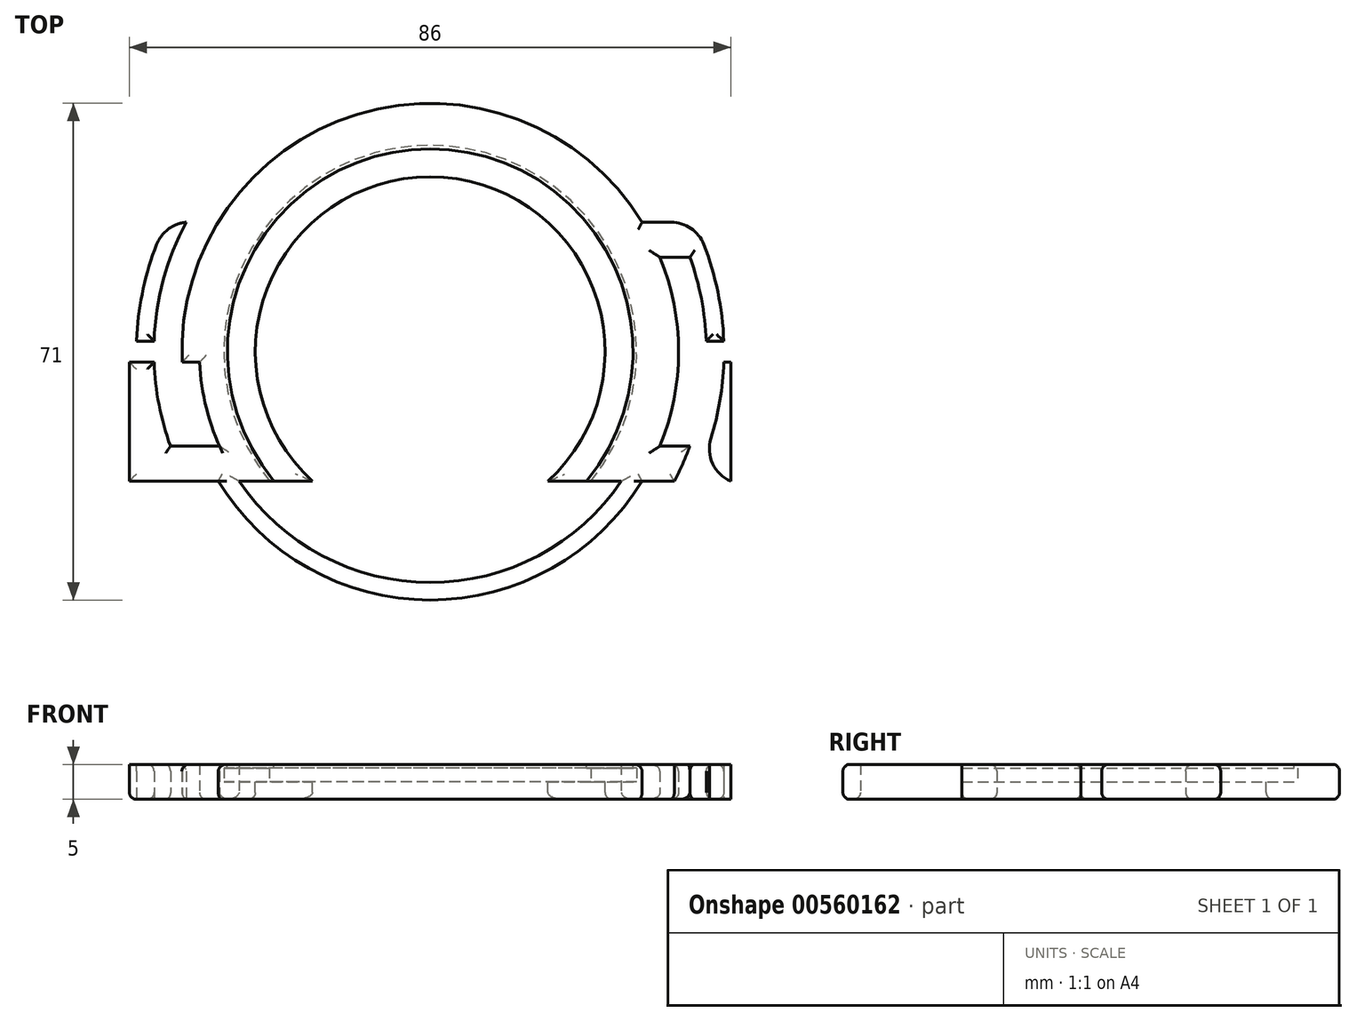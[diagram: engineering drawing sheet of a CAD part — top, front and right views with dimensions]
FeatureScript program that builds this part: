
annotation { "Feature Type Name" : "Feature", "Feature Type Description" : "" }
export const myFeature = defineFeature(function(context is Context, id is Id, definition is map)
    precondition{}
    {
        {
            var Q0;
            Q0=qCreatedBy(makeId("Top.planeOp"),FACE);
            var sketch = newSketch(context, id + "F0", { "sketchPlane" : qUnion([Q0])});
            skCircle(sketch, "E0", {"center": v(0, 0) * mm, "radius": 33 * mm});
            skLineSegment(sketch, "E1.bottom", {"start": v(43, -18.5) * mm, "end": v(-43, -18.5) * mm});
            skLineSegment(sketch, "E1.top", {"start": v(43, 18.5) * mm, "end": v(-43, 18.5) * mm});
            skLineSegment(sketch, "E1.left", {"start": v(43, -18.5) * mm, "end": v(43, 18.5) * mm});
            skLineSegment(sketch, "E1.right", {"start": v(-43, -18.5) * mm, "end": v(-43, 18.5) * mm});
            skCircle(sketch, "E2", {"center": v(0, 0) * mm, "radius": 42 * mm});
            skCircle(sketch, "E3", {"center": v(0, 0) * mm, "radius": 35.5 * mm});
            skCircle(sketch, "E4", {"center": v(0, 0) * mm, "radius": 39.5 * mm});
            skLineSegment(sketch, "E5.bottom", {"start": v(38.5, 13.5) * mm, "end": v(-38.5, 13.5) * mm});
            skLineSegment(sketch, "E5.top", {"start": v(38.5, -13.5) * mm, "end": v(-38.5, -13.5) * mm});
            skLineSegment(sketch, "E5.left", {"start": v(38.5, 13.5) * mm, "end": v(38.5, -13.5) * mm});
            skLineSegment(sketch, "E5.right", {"start": v(-38.5, 13.5) * mm, "end": v(-38.5, -13.5) * mm});
            skLineSegment(sketch, "E6.bottom", {"start": v(50, 1.5) * mm, "end": v(-50, 1.5) * mm});
            skLineSegment(sketch, "E6.top", {"start": v(50, -1.5) * mm, "end": v(-50, -1.5) * mm});
            skLineSegment(sketch, "E6.left", {"start": v(50, 1.5) * mm, "end": v(50, -1.5) * mm});
            skLineSegment(sketch, "E6.right", {"start": v(-50, 1.5) * mm, "end": v(-50, -1.5) * mm});
            skSolve(sketch);
        }
        {
            var Q0;
            {var subQ6=sQuery(id+"F0.wireOp",EDGE,"E1.bottom");var subQ14=sQuery(id+"F0.wireOp",EDGE,"E2");var subQ16=makeQuery(id+"F0.imprint","INTERSECT",VERTEX,{"disambiguationData":[OD(1.0)],"derivedFrom":[subQ6,subQ14]});Q0=makeQuery(id+"F0.imprint","IMPRINT",FACE,{"disambiguationData":[TD([[makeQuery(id+"F0.imprint","IMPRINT",EDGE,{"disambiguationData":[TD([[subQ16,1.0]])],"derivedFrom":subQ6}),-1.0]])]});}
            var Q1;
            {var subQ0=sQuery(id+"F0.wireOp",EDGE,"E5.bottom");var subQ1=sQuery(id+"F0.wireOp",EDGE,"E4");var subQ2=makeQuery(id+"F0.imprint","INTERSECT",VERTEX,{"disambiguationData":[OD(1.0)],"derivedFrom":[subQ1,subQ0]});Q1=makeQuery(id+"F0.imprint","IMPRINT",FACE,{"disambiguationData":[TD([[makeQuery(id+"F0.imprint","IMPRINT",EDGE,{"disambiguationData":[TD([[subQ2,-1.0]])],"derivedFrom":subQ1}),-1.0]])]});}
            var Q2;
            {var subQ0=sQuery(id+"F0.wireOp",EDGE,"E5.right");var subQ1=sQuery(id+"F0.wireOp",EDGE,"E4");var subQ2=makeQuery(id+"F0.imprint","INTERSECT",VERTEX,{"disambiguationData":[OD(1.0)],"derivedFrom":[subQ1,subQ0]});Q2=makeQuery(id+"F0.imprint","IMPRINT",FACE,{"disambiguationData":[TD([[makeQuery(id+"F0.imprint","IMPRINT",EDGE,{"disambiguationData":[TD([[subQ2,-1.0]])],"derivedFrom":subQ1}),-1.0]])]});}
            var Q3;
            {var subQ0=sQuery(id+"F0.wireOp",EDGE,"E3");var subQ1=sQuery(id+"F0.wireOp",EDGE,"E1.top");var subQ2=makeQuery(id+"F0.imprint","INTERSECT",VERTEX,{"disambiguationData":[OD(1.0)],"derivedFrom":[subQ1,subQ0]});Q3=makeQuery(id+"F0.imprint","IMPRINT",FACE,{"disambiguationData":[TD([[makeQuery(id+"F0.imprint","IMPRINT",EDGE,{"disambiguationData":[TD([[subQ2,-1.0]])],"derivedFrom":subQ1}),1.0]])]});}
            var Q4;
            {var subQ0=sQuery(id+"F0.wireOp",EDGE,"E3");var subQ1=sQuery(id+"F0.wireOp",EDGE,"E1.bottom");var subQ2=makeQuery(id+"F0.imprint","INTERSECT",VERTEX,{"disambiguationData":[OD(1.0)],"derivedFrom":[subQ1,subQ0]});Q4=makeQuery(id+"F0.imprint","IMPRINT",FACE,{"disambiguationData":[TD([[makeQuery(id+"F0.imprint","IMPRINT",EDGE,{"disambiguationData":[TD([[subQ2,-1.0]])],"derivedFrom":subQ1}),-1.0]])]});}
            var Q5;
            {var subQ0=sQuery(id+"F0.wireOp",EDGE,"E5.bottom");var subQ1=sQuery(id+"F0.wireOp",EDGE,"E0");var subQ2=makeQuery(id+"F0.imprint","INTERSECT",VERTEX,{"disambiguationData":[OD(1.0)],"derivedFrom":[subQ1,subQ0]});Q5=makeQuery(id+"F0.imprint","IMPRINT",FACE,{"disambiguationData":[TD([[makeQuery(id+"F0.imprint","IMPRINT",EDGE,{"disambiguationData":[TD([[subQ2,-1.0]])],"derivedFrom":subQ1}),-1.0]])]});}
            var Q6;
            {var subQ0=sQuery(id+"F0.wireOp",EDGE,"E5.top");var subQ1=sQuery(id+"F0.wireOp",EDGE,"E0");var subQ2=makeQuery(id+"F0.imprint","INTERSECT",VERTEX,{"disambiguationData":[OD(0.0)],"derivedFrom":[subQ1,subQ0]});Q6=makeQuery(id+"F0.imprint","IMPRINT",FACE,{"disambiguationData":[TD([[makeQuery(id+"F0.imprint","IMPRINT",EDGE,{"disambiguationData":[TD([[subQ2,-1.0]])],"derivedFrom":subQ1}),-1.0]])]});}
            var Q7;
            {var subQ0=sQuery(id+"F0.wireOp",EDGE,"E1.top");var subQ1=sQuery(id+"F0.wireOp",EDGE,"E0");var subQ2=makeQuery(id+"F0.imprint","INTERSECT",VERTEX,{"disambiguationData":[OD(1.0)],"derivedFrom":[subQ1,subQ0]});Q7=makeQuery(id+"F0.imprint","IMPRINT",FACE,{"disambiguationData":[TD([[makeQuery(id+"F0.imprint","IMPRINT",EDGE,{"disambiguationData":[TD([[subQ2,-1.0]])],"derivedFrom":subQ1}),-1.0]])]});}
            var Q8;
            {var subQ0=sQuery(id+"F0.wireOp",EDGE,"E1.bottom");var subQ1=sQuery(id+"F0.wireOp",EDGE,"E0");var subQ2=makeQuery(id+"F0.imprint","INTERSECT",VERTEX,{"disambiguationData":[OD(0.0)],"derivedFrom":[subQ1,subQ0]});Q8=makeQuery(id+"F0.imprint","IMPRINT",FACE,{"disambiguationData":[TD([[makeQuery(id+"F0.imprint","IMPRINT",EDGE,{"disambiguationData":[TD([[subQ2,-1.0]])],"derivedFrom":subQ1}),-1.0]])]});}
            var Q9;
            {var subQ0=sQuery(id+"F0.wireOp",EDGE,"E1.top");var subQ1=sQuery(id+"F0.wireOp",EDGE,"E0");var subQ2=makeQuery(id+"F0.imprint","INTERSECT",VERTEX,{"disambiguationData":[OD(0.0)],"derivedFrom":[subQ1,subQ0]});Q9=makeQuery(id+"F0.imprint","IMPRINT",FACE,{"disambiguationData":[TD([[makeQuery(id+"F0.imprint","IMPRINT",EDGE,{"disambiguationData":[TD([[subQ2,-1.0]])],"derivedFrom":subQ1}),-1.0]])]});}
            var Q10;
            {var subQ0=sQuery(id+"F0.wireOp",EDGE,"E1.top");var subQ1=sQuery(id+"F0.wireOp",EDGE,"E0");var subQ2=makeQuery(id+"F0.imprint","INTERSECT",VERTEX,{"disambiguationData":[OD(0.0)],"derivedFrom":[subQ1,subQ0]});Q10=makeQuery(id+"F0.imprint","IMPRINT",FACE,{"disambiguationData":[TD([[makeQuery(id+"F0.imprint","IMPRINT",EDGE,{"disambiguationData":[TD([[subQ2,-1.0]])],"derivedFrom":subQ1}),1.0]])]});}
            var Q11;
            {var subQ0=sQuery(id+"F0.wireOp",EDGE,"E1.top");var subQ1=sQuery(id+"F0.wireOp",EDGE,"E0");var subQ2=makeQuery(id+"F0.imprint","INTERSECT",VERTEX,{"disambiguationData":[OD(0.0)],"derivedFrom":[subQ1,subQ0]});Q11=makeQuery(id+"F0.imprint","IMPRINT",FACE,{"disambiguationData":[TD([[makeQuery(id+"F0.imprint","IMPRINT",EDGE,{"disambiguationData":[TD([[subQ2,1.0]])],"derivedFrom":subQ1}),1.0]])]});}
            var Q12;
            {var subQ0=sQuery(id+"F0.wireOp",EDGE,"E5.bottom");var subQ1=sQuery(id+"F0.wireOp",EDGE,"E0");var subQ2=makeQuery(id+"F0.imprint","INTERSECT",VERTEX,{"disambiguationData":[OD(1.0)],"derivedFrom":[subQ1,subQ0]});Q12=makeQuery(id+"F0.imprint","IMPRINT",FACE,{"disambiguationData":[TD([[makeQuery(id+"F0.imprint","IMPRINT",EDGE,{"disambiguationData":[TD([[subQ2,-1.0]])],"derivedFrom":subQ1}),1.0]])]});}
            var Q13;
            {var subQ0=sQuery(id+"F0.wireOp",EDGE,"E5.top");var subQ1=sQuery(id+"F0.wireOp",EDGE,"E0");var subQ2=makeQuery(id+"F0.imprint","INTERSECT",VERTEX,{"disambiguationData":[OD(0.0)],"derivedFrom":[subQ1,subQ0]});Q13=makeQuery(id+"F0.imprint","IMPRINT",FACE,{"disambiguationData":[TD([[makeQuery(id+"F0.imprint","IMPRINT",EDGE,{"disambiguationData":[TD([[subQ2,-1.0]])],"derivedFrom":subQ1}),1.0]])]});}
            var Q14;
            {var subQ0=sQuery(id+"F0.wireOp",EDGE,"E1.bottom");var subQ1=sQuery(id+"F0.wireOp",EDGE,"E0");var subQ2=makeQuery(id+"F0.imprint","INTERSECT",VERTEX,{"disambiguationData":[OD(0.0)],"derivedFrom":[subQ1,subQ0]});Q14=makeQuery(id+"F0.imprint","IMPRINT",FACE,{"disambiguationData":[TD([[makeQuery(id+"F0.imprint","IMPRINT",EDGE,{"disambiguationData":[TD([[subQ2,-1.0]])],"derivedFrom":subQ1}),1.0]])]});}
            var Q15;
            {var subQ0=sQuery(id+"F0.wireOp",EDGE,"E5.bottom");var subQ1=sQuery(id+"F0.wireOp",EDGE,"E4");var subQ2=makeQuery(id+"F0.imprint","INTERSECT",VERTEX,{"disambiguationData":[OD(0.0)],"derivedFrom":[subQ1,subQ0]});Q15=makeQuery(id+"F0.imprint","IMPRINT",FACE,{"disambiguationData":[TD([[makeQuery(id+"F0.imprint","IMPRINT",EDGE,{"disambiguationData":[TD([[subQ2,1.0]])],"derivedFrom":subQ1}),-1.0]])]});}
            var Q16;
            {var subQ0=sQuery(id+"F0.wireOp",EDGE,"E1.top");var subQ1=sQuery(id+"F0.wireOp",EDGE,"E0");var subQ2=makeQuery(id+"F0.imprint","INTERSECT",VERTEX,{"disambiguationData":[OD(0.0)],"derivedFrom":[subQ1,subQ0]});Q16=makeQuery(id+"F0.imprint","IMPRINT",FACE,{"disambiguationData":[TD([[makeQuery(id+"F0.imprint","IMPRINT",EDGE,{"disambiguationData":[TD([[subQ2,1.0]])],"derivedFrom":subQ1}),-1.0]])]});}
            var Q17;
            {var subQ0=sQuery(id+"F0.wireOp",EDGE,"E4");var subQ1=sQuery(id+"F0.wireOp",EDGE,"E1.top");var subQ2=makeQuery(id+"F0.imprint","INTERSECT",VERTEX,{"disambiguationData":[OD(0.0)],"derivedFrom":[subQ1,subQ0]});Q17=makeQuery(id+"F0.imprint","IMPRINT",FACE,{"disambiguationData":[TD([[makeQuery(id+"F0.imprint","IMPRINT",EDGE,{"disambiguationData":[TD([[subQ2,-1.0]])],"derivedFrom":subQ1}),1.0]])]});}
            var Q18;
            {var subQ0=sQuery(id+"F0.wireOp",EDGE,"E5.top");var subQ1=sQuery(id+"F0.wireOp",EDGE,"E4");var subQ2=makeQuery(id+"F0.imprint","INTERSECT",VERTEX,{"disambiguationData":[OD(1.0)],"derivedFrom":[subQ1,subQ0]});Q18=makeQuery(id+"F0.imprint","IMPRINT",FACE,{"disambiguationData":[TD([[makeQuery(id+"F0.imprint","IMPRINT",EDGE,{"disambiguationData":[TD([[subQ2,-1.0]])],"derivedFrom":subQ1}),-1.0]])]});}
            var Q19;
            {var subQ6=sQuery(id+"F0.wireOp",EDGE,"E2");var subQ7=sQuery(id+"F0.wireOp",EDGE,"E1.bottom");var subQ8=makeQuery(id+"F0.imprint","INTERSECT",VERTEX,{"disambiguationData":[OD(0.0)],"derivedFrom":[subQ7,subQ6]});Q19=makeQuery(id+"F0.imprint","IMPRINT",FACE,{"disambiguationData":[TD([[makeQuery(id+"F0.imprint","IMPRINT",EDGE,{"disambiguationData":[TD([[subQ8,-1.0]])],"derivedFrom":subQ7}),-1.0]])]});}
            var Q20;
            {var subQ0=sQuery(id+"F0.wireOp",EDGE,"E1.bottom");var subQ1=sQuery(id+"F0.wireOp",EDGE,"E0");var subQ2=makeQuery(id+"F0.imprint","INTERSECT",VERTEX,{"disambiguationData":[OD(1.0)],"derivedFrom":[subQ1,subQ0]});Q20=makeQuery(id+"F0.imprint","IMPRINT",FACE,{"disambiguationData":[TD([[makeQuery(id+"F0.imprint","IMPRINT",EDGE,{"disambiguationData":[TD([[subQ2,-1.0]])],"derivedFrom":subQ1}),-1.0]])]});}
            var Q21;
            {var subQ0=sQuery(id+"F0.wireOp",EDGE,"E4");var subQ1=sQuery(id+"F0.wireOp",EDGE,"E1.bottom");var subQ2=makeQuery(id+"F0.imprint","INTERSECT",VERTEX,{"disambiguationData":[OD(0.0)],"derivedFrom":[subQ1,subQ0]});Q21=makeQuery(id+"F0.imprint","IMPRINT",FACE,{"disambiguationData":[TD([[makeQuery(id+"F0.imprint","IMPRINT",EDGE,{"disambiguationData":[TD([[subQ2,-1.0]])],"derivedFrom":subQ1}),-1.0]])]});}
            var Q22;
            {var subQ0=sQuery(id+"F0.wireOp",EDGE,"E5.bottom");var subQ1=sQuery(id+"F0.wireOp",EDGE,"E0");var subQ2=makeQuery(id+"F0.imprint","INTERSECT",VERTEX,{"disambiguationData":[OD(0.0)],"derivedFrom":[subQ1,subQ0]});Q22=makeQuery(id+"F0.imprint","IMPRINT",FACE,{"disambiguationData":[TD([[makeQuery(id+"F0.imprint","IMPRINT",EDGE,{"disambiguationData":[TD([[subQ2,1.0]])],"derivedFrom":subQ1}),-1.0]])]});}
            var Q23;
            {var subQ5=sQuery(id+"F0.wireOp",EDGE,"E2");var subQ7=sQuery(id+"F0.wireOp",EDGE,"E1.top");var subQ11=makeQuery(id+"F0.imprint","INTERSECT",VERTEX,{"disambiguationData":[OD(1.0)],"derivedFrom":[subQ7,subQ5]});Q23=makeQuery(id+"F0.imprint","IMPRINT",FACE,{"disambiguationData":[TD([[makeQuery(id+"F0.imprint","IMPRINT",EDGE,{"disambiguationData":[TD([[subQ11,1.0]])],"derivedFrom":subQ7}),1.0]])]});}
            var Q24;
            {var subQ0=sQuery(id+"F0.wireOp",EDGE,"E6.bottom");var subQ1=sQuery(id+"F0.wireOp",EDGE,"E0");var subQ2=makeQuery(id+"F0.imprint","INTERSECT",VERTEX,{"disambiguationData":[OD(1.0)],"derivedFrom":[subQ1,subQ0]});Q24=makeQuery(id+"F0.imprint","IMPRINT",FACE,{"disambiguationData":[TD([[makeQuery(id+"F0.imprint","IMPRINT",EDGE,{"disambiguationData":[TD([[subQ2,-1.0]])],"derivedFrom":subQ1}),-1.0]])]});}
            var Q25;
            {var subQ0=sQuery(id+"F0.wireOp",EDGE,"E6.top");var subQ1=sQuery(id+"F0.wireOp",EDGE,"E0");var subQ2=makeQuery(id+"F0.imprint","INTERSECT",VERTEX,{"disambiguationData":[OD(0.0)],"derivedFrom":[subQ1,subQ0]});Q25=makeQuery(id+"F0.imprint","IMPRINT",FACE,{"disambiguationData":[TD([[makeQuery(id+"F0.imprint","IMPRINT",EDGE,{"disambiguationData":[TD([[subQ2,-1.0]])],"derivedFrom":subQ1}),-1.0]])]});}
            var Q26;
            {var subQ0=sQuery(id+"F0.wireOp",EDGE,"E6.bottom");var subQ1=sQuery(id+"F0.wireOp",EDGE,"E0");var subQ2=makeQuery(id+"F0.imprint","INTERSECT",VERTEX,{"disambiguationData":[OD(1.0)],"derivedFrom":[subQ1,subQ0]});Q26=makeQuery(id+"F0.imprint","IMPRINT",FACE,{"disambiguationData":[TD([[makeQuery(id+"F0.imprint","IMPRINT",EDGE,{"disambiguationData":[TD([[subQ2,-1.0]])],"derivedFrom":subQ1}),1.0]])]});}
            var Q27;
            {var subQ0=sQuery(id+"F0.wireOp",EDGE,"E6.top");var subQ1=sQuery(id+"F0.wireOp",EDGE,"E0");var subQ2=makeQuery(id+"F0.imprint","INTERSECT",VERTEX,{"disambiguationData":[OD(0.0)],"derivedFrom":[subQ1,subQ0]});Q27=makeQuery(id+"F0.imprint","IMPRINT",FACE,{"disambiguationData":[TD([[makeQuery(id+"F0.imprint","IMPRINT",EDGE,{"disambiguationData":[TD([[subQ2,-1.0]])],"derivedFrom":subQ1}),1.0]])]});}
            var Q28;
            {var subQ0=sQuery(id+"F0.wireOp",EDGE,"E6.bottom");var subQ1=sQuery(id+"F0.wireOp",EDGE,"E0");var subQ2=makeQuery(id+"F0.imprint","INTERSECT",VERTEX,{"disambiguationData":[OD(0.0)],"derivedFrom":[subQ1,subQ0]});Q28=makeQuery(id+"F0.imprint","IMPRINT",FACE,{"disambiguationData":[TD([[makeQuery(id+"F0.imprint","IMPRINT",EDGE,{"disambiguationData":[TD([[subQ2,1.0]])],"derivedFrom":subQ1}),-1.0]])]});}
            var Q29;
            {var subQ0=sQuery(id+"F0.wireOp",EDGE,"E5.top");var subQ1=sQuery(id+"F0.wireOp",EDGE,"E0");var subQ2=makeQuery(id+"F0.imprint","INTERSECT",VERTEX,{"disambiguationData":[OD(1.0)],"derivedFrom":[subQ1,subQ0]});Q29=makeQuery(id+"F0.imprint","IMPRINT",FACE,{"disambiguationData":[TD([[makeQuery(id+"F0.imprint","IMPRINT",EDGE,{"disambiguationData":[TD([[subQ2,-1.0]])],"derivedFrom":subQ1}),-1.0]])]});}
            var Q30;
            {var subQ1=sQuery(id+"F0.wireOp",EDGE,"E1.top");var subQ5=sQuery(id+"F0.wireOp",EDGE,"E2");var subQ6=makeQuery(id+"F0.imprint","INTERSECT",VERTEX,{"disambiguationData":[OD(0.0)],"derivedFrom":[subQ1,subQ5]});Q30=makeQuery(id+"F0.imprint","IMPRINT",FACE,{"disambiguationData":[TD([[makeQuery(id+"F0.imprint","IMPRINT",EDGE,{"disambiguationData":[TD([[subQ6,-1.0]])],"derivedFrom":subQ1}),1.0]])]});}
            extrude(context, id + "F1", {"entities" : qUnion([Q0, Q1, Q2, Q3, Q4, Q5, Q6, Q7, Q8, Q9, Q10, Q11, Q12, Q13, Q14, Q15, Q16, Q17, Q18, Q19, Q20, Q21, Q22, Q23, Q24, Q25, Q26, Q27, Q28, Q29, Q30]), "depth" : 5 * mm, "offsetDistance" : 25 * mm});
        }
        {
            var Q0;
            Q0=makeQuery(id+"F1.opExtrude","CAP_FACE",FACE,{"disambiguationData":[OSD([sQuery(id+"F0.wireOp",EDGE,"E1.bottom"),sQuery(id+"F0.wireOp",EDGE,"E1.top"),sQuery(id+"F0.wireOp",EDGE,"E2"),sQuery(id+"F0.wireOp",EDGE,"E3"),sQuery(id+"F0.wireOp",EDGE,"E4"),sQuery(id+"F0.wireOp",EDGE,"E5.bottom"),sQuery(id+"F0.wireOp",EDGE,"E5.top")])],"isStart":false});
            var sketch = newSketch(context, id + "F2", { "sketchPlane" : qUnion([Q0])});
            skCircle(sketch, "E7", {"center": v(0, 0) * mm, "radius": 29 * mm});
            skSolve(sketch);
        }
        {
            var Q0;
            Q0 = qSketchRegion(id + "F2", true);
            extrude(context, id + "F3", {"entities" : qUnion([Q0]), "operationType" : NewBodyOperationType.REMOVE, "oppositeDirection" : true, "depth" : 2.5 * mm, "offsetDistance" : 25 * mm});
        }
        {
            var Q0;
            {var subQ0=sQuery(id+"F0.wireOp",EDGE,"E2");var subQ1=sQuery(id+"F0.wireOp",EDGE,"E1.bottom");Q0=makeQuery(id+"F1.opExtrude","SWEPT_EDGE",EDGE,{"disambiguationData":[OSD([subQ1,subQ0]),TDD([makeQuery(id+"F0.imprint","INTERSECT",VERTEX,{"disambiguationData":[OD(1.0)],"derivedFrom":[subQ1,subQ0]})])]});}
            var Q1;
            {var subQ0=sQuery(id+"F0.wireOp",EDGE,"E2");var subQ1=sQuery(id+"F0.wireOp",EDGE,"E1.bottom");Q1=makeQuery(id+"F1.opExtrude","SWEPT_EDGE",EDGE,{"disambiguationData":[OSD([subQ1,subQ0]),TDD([makeQuery(id+"F0.imprint","INTERSECT",VERTEX,{"disambiguationData":[OD(0.0)],"derivedFrom":[subQ1,subQ0]})])]});}
            var Q2;
            {var subQ0=sQuery(id+"F0.wireOp",EDGE,"E2");var subQ1=sQuery(id+"F0.wireOp",EDGE,"E1.top");Q2=makeQuery(id+"F1.opExtrude","SWEPT_EDGE",EDGE,{"disambiguationData":[OSD([subQ1,subQ0]),TDD([makeQuery(id+"F0.imprint","INTERSECT",VERTEX,{"disambiguationData":[OD(0.0)],"derivedFrom":[subQ1,subQ0]})])]});}
            var Q3;
            {var subQ0=sQuery(id+"F0.wireOp",EDGE,"E2");var subQ1=sQuery(id+"F0.wireOp",EDGE,"E1.top");Q3=makeQuery(id+"F1.opExtrude","SWEPT_EDGE",EDGE,{"disambiguationData":[OSD([subQ1,subQ0]),TDD([makeQuery(id+"F0.imprint","INTERSECT",VERTEX,{"disambiguationData":[OD(1.0)],"derivedFrom":[subQ1,subQ0]})])]});}
            fillet(context, id + "F4", {"entities" : qUnion([Q0, Q1, Q2, Q3]), "radius" : 5 * mm, "tangentPropagation" : true, "allowEdgeOverflow" : false});
        }
        {
            var Q0;
            Q0=makeQuery(id+"F3.boolean.opBoolean","COPY",FACE,{"derivedFrom":makeQuery(id+"F3.opExtrude","CAP_FACE",FACE,{"disambiguationData":[OSD([sQuery(id+"F2.wireOp",EDGE,"E7")])],"isStart":false})});
            var sketch = newSketch(context, id + "F5", { "sketchPlane" : qUnion([Q0])});
            skCircle(sketch, "E8", {"center": v(0, 0) * mm, "radius": 29.5 * mm});
            skSolve(sketch);
        }
        {
            var Q0;
            Q0 = qSketchRegion(id + "F5", true);
            extrude(context, id + "F6", {"entities" : qUnion([Q0]), "operationType" : NewBodyOperationType.REMOVE, "depth" : 2 * mm, "offsetDistance" : 25 * mm});
        }
        {
            var Q0;
            Q0=makeQuery(id+"F6.boolean.opBoolean","MERGE",FACE,{"derivedFrom":[makeQuery(id+"F3.boolean.opBoolean","COPY",FACE,{"derivedFrom":makeQuery(id+"F3.opExtrude","CAP_FACE",FACE,{"disambiguationData":[OSD([sQuery(id+"F2.wireOp",EDGE,"E7")])],"isStart":false})}),makeQuery(id+"F6.opExtrude","CAP_FACE",FACE,{"disambiguationData":[OSD([sQuery(id+"F5.wireOp",EDGE,"E8")])],"isStart":true})]});
            var sketch = newSketch(context, id + "F7", { "sketchPlane" : qUnion([Q0])});
            skPoint(sketch, "E9", {"position": v(0, 0) * mm});
            skSolve(sketch);
        }
        {
            var Q0;
            Q0=sQuery(id+"F7.wireOp",VERTEX,"E9");
            var Q1;
            Q1=makeQuery(id+"F1.opExtrude","SWEPT_BODY",BODY,{"disambiguationData":[OSD([sQuery(id+"F0.wireOp",EDGE,"E1.bottom"),sQuery(id+"F0.wireOp",EDGE,"E1.top"),sQuery(id+"F0.wireOp",EDGE,"E2"),sQuery(id+"F0.wireOp",EDGE,"E3"),sQuery(id+"F0.wireOp",EDGE,"E4"),sQuery(id+"F0.wireOp",EDGE,"E5.bottom"),sQuery(id+"F0.wireOp",EDGE,"E5.top")])]});
            hole(context, id + "F8", {"style" : HoleStyle.SIMPLE, "endStyle" : HoleEndStyle.THROUGH, "holeDiameter" : 50 * mm, "isTappedThrough" : true, "tappedDepth" : 12 * mm, "tapClearance" : 3, "locations" : qUnion([Q0]), "scope" : qUnion([Q1])});
        }
        {
            var Q0;
            {var subQ0=sQuery(id+"F0.wireOp",EDGE,"E3");var subQ1=sQuery(id+"F0.wireOp",EDGE,"E1.top");Q0=makeQuery(id+"F1.opExtrude","CAP_EDGE",EDGE,{"disambiguationData":[OSD([subQ0]),TDD([makeQuery(id+"F0.imprint","IMPRINT",EDGE,{"disambiguationData":[TD([[makeQuery(id+"F0.imprint","INTERSECT",VERTEX,{"disambiguationData":[OD(0.0)],"derivedFrom":[subQ1,subQ0]}),-1.0]])],"derivedFrom":subQ0})])],"isStart":false});}
            var Q1;
            {var subQ0=sQuery(id+"F0.wireOp",EDGE,"E1.top");Q1=makeQuery(id+"F1.opExtrude","CAP_EDGE",EDGE,{"disambiguationData":[OSD([subQ0]),TDD([makeQuery(id+"F0.imprint","IMPRINT",EDGE,{"disambiguationData":[TD([[makeQuery(id+"F0.imprint","INTERSECT",VERTEX,{"disambiguationData":[OD(1.0)],"derivedFrom":[subQ0,sQuery(id+"F0.wireOp",EDGE,"E3")]}),-1.0]])],"derivedFrom":subQ0}),makeQuery(id+"F0.imprint","IMPRINT",EDGE,{"disambiguationData":[TD([[makeQuery(id+"F0.imprint","INTERSECT",VERTEX,{"disambiguationData":[OD(1.0)],"derivedFrom":[subQ0,sQuery(id+"F0.wireOp",EDGE,"E2")]}),1.0]])],"derivedFrom":subQ0})])],"isStart":false});}
            var Q2;
            {var subQ0=sQuery(id+"F0.wireOp",EDGE,"E3");var subQ1=sQuery(id+"F0.wireOp",EDGE,"E1.bottom");Q2=makeQuery(id+"F1.opExtrude","CAP_EDGE",EDGE,{"disambiguationData":[OSD([subQ0]),TDD([makeQuery(id+"F0.imprint","IMPRINT",EDGE,{"disambiguationData":[TD([[makeQuery(id+"F0.imprint","INTERSECT",VERTEX,{"disambiguationData":[OD(0.0)],"derivedFrom":[subQ1,subQ0]}),1.0]])],"derivedFrom":subQ0})])],"isStart":false});}
            var Q3;
            {var subQ0=sQuery(id+"F0.wireOp",EDGE,"E1.top");var subQ1=makeQuery(id+"F0.imprint","INTERSECT",VERTEX,{"disambiguationData":[OD(0.0)],"derivedFrom":[subQ0,sQuery(id+"F0.wireOp",EDGE,"E4")]});Q3=makeQuery(id+"F1.opExtrude","CAP_EDGE",EDGE,{"disambiguationData":[OSD([subQ0]),TDD([makeQuery(id+"F0.imprint","IMPRINT",EDGE,{"disambiguationData":[TD([[makeQuery(id+"F0.imprint","INTERSECT",VERTEX,{"disambiguationData":[OD(0.0)],"derivedFrom":[subQ0,sQuery(id+"F0.wireOp",EDGE,"E2")]}),-1.0]])],"derivedFrom":subQ0}),makeQuery(id+"F0.imprint","IMPRINT",EDGE,{"disambiguationData":[TD([[subQ1,-1.0]])],"derivedFrom":subQ0})])],"isStart":false});}
            var Q4;
            {var subQ0=sQuery(id+"F0.wireOp",EDGE,"E3");Q4=makeQuery(id+"F1.opExtrude","CAP_EDGE",EDGE,{"disambiguationData":[OSD([subQ0]),TDD([makeQuery(id+"F0.imprint","IMPRINT",EDGE,{"disambiguationData":[TD([[makeQuery(id+"F0.imprint","INTERSECT",VERTEX,{"disambiguationData":[OD(1.0)],"derivedFrom":[subQ0,sQuery(id+"F0.wireOp",EDGE,"E5.bottom")]}),-1.0]])],"derivedFrom":subQ0})])],"isStart":false});}
            var Q5;
            {var subQ0=sQuery(id+"F0.wireOp",EDGE,"E5.bottom");Q5=makeQuery(id+"F1.opExtrude","CAP_EDGE",EDGE,{"disambiguationData":[OSD([subQ0]),TDD([makeQuery(id+"F0.imprint","IMPRINT",EDGE,{"disambiguationData":[TD([[makeQuery(id+"F0.imprint","INTERSECT",VERTEX,{"disambiguationData":[OD(1.0)],"derivedFrom":[sQuery(id+"F0.wireOp",EDGE,"E3"),subQ0]}),-1.0]])],"derivedFrom":subQ0})])],"isStart":false});}
            var Q6;
            {var subQ0=sQuery(id+"F0.wireOp",EDGE,"E5.right");var subQ1=sQuery(id+"F0.wireOp",EDGE,"E4");var subQ2=makeQuery(id+"F0.imprint","INTERSECT",VERTEX,{"disambiguationData":[OD(1.0)],"derivedFrom":[subQ1,subQ0]});var subQ3=makeQuery(id+"F0.imprint","INTERSECT",VERTEX,{"disambiguationData":[OD(0.0)],"derivedFrom":[subQ1,subQ0]});Q6=makeQuery(id+"F1.opExtrude","CAP_EDGE",EDGE,{"disambiguationData":[OSD([subQ1]),TDD([makeQuery(id+"F0.imprint","IMPRINT",EDGE,{"disambiguationData":[TD([[makeQuery(id+"F0.imprint","INTERSECT",VERTEX,{"disambiguationData":[OD(1.0)],"derivedFrom":[subQ1,sQuery(id+"F0.wireOp",EDGE,"E5.bottom")]}),-1.0]])],"derivedFrom":subQ1}),makeQuery(id+"F0.imprint","IMPRINT",EDGE,{"disambiguationData":[TD([[subQ3,-1.0]])],"derivedFrom":subQ1}),makeQuery(id+"F0.imprint","IMPRINT",EDGE,{"disambiguationData":[TD([[subQ2,-1.0]])],"derivedFrom":subQ1})])],"isStart":false});}
            var Q7;
            {var subQ0=sQuery(id+"F0.wireOp",EDGE,"E5.top");Q7=makeQuery(id+"F1.opExtrude","CAP_EDGE",EDGE,{"disambiguationData":[OSD([subQ0]),TDD([makeQuery(id+"F0.imprint","IMPRINT",EDGE,{"disambiguationData":[TD([[makeQuery(id+"F0.imprint","INTERSECT",VERTEX,{"disambiguationData":[OD(0.0)],"derivedFrom":[sQuery(id+"F0.wireOp",EDGE,"E3"),subQ0]}),-1.0]])],"derivedFrom":subQ0})])],"isStart":false});}
            var Q8;
            {var subQ0=sQuery(id+"F0.wireOp",EDGE,"E5.left");var subQ1=sQuery(id+"F0.wireOp",EDGE,"E4");var subQ2=makeQuery(id+"F0.imprint","INTERSECT",VERTEX,{"disambiguationData":[OD(0.0)],"derivedFrom":[subQ1,subQ0]});Q8=makeQuery(id+"F1.opExtrude","CAP_EDGE",EDGE,{"disambiguationData":[OSD([subQ1]),TDD([makeQuery(id+"F0.imprint","IMPRINT",EDGE,{"disambiguationData":[TD([[makeQuery(id+"F0.imprint","INTERSECT",VERTEX,{"disambiguationData":[OD(0.0)],"derivedFrom":[subQ1,sQuery(id+"F0.wireOp",EDGE,"E5.bottom")]}),1.0]])],"derivedFrom":subQ1}),makeQuery(id+"F0.imprint","IMPRINT",EDGE,{"disambiguationData":[TD([[makeQuery(id+"F0.imprint","INTERSECT",VERTEX,{"disambiguationData":[OD(1.0)],"derivedFrom":[subQ1,sQuery(id+"F0.wireOp",EDGE,"E5.top")]}),-1.0]])],"derivedFrom":subQ1}),makeQuery(id+"F0.imprint","IMPRINT",EDGE,{"disambiguationData":[TD([[subQ2,1.0]])],"derivedFrom":subQ1})])],"isStart":false});}
            var Q9;
            {var subQ0=sQuery(id+"F0.wireOp",EDGE,"E5.bottom");Q9=makeQuery(id+"F1.opExtrude","CAP_EDGE",EDGE,{"disambiguationData":[OSD([subQ0]),TDD([makeQuery(id+"F0.imprint","IMPRINT",EDGE,{"disambiguationData":[TD([[makeQuery(id+"F0.imprint","INTERSECT",VERTEX,{"disambiguationData":[OD(0.0)],"derivedFrom":[sQuery(id+"F0.wireOp",EDGE,"E3"),subQ0]}),1.0]])],"derivedFrom":subQ0})])],"isStart":false});}
            var Q10;
            {var subQ0=sQuery(id+"F0.wireOp",EDGE,"E3");Q10=makeQuery(id+"F1.opExtrude","CAP_EDGE",EDGE,{"disambiguationData":[OSD([subQ0]),TDD([makeQuery(id+"F0.imprint","IMPRINT",EDGE,{"disambiguationData":[TD([[makeQuery(id+"F0.imprint","INTERSECT",VERTEX,{"disambiguationData":[OD(0.0)],"derivedFrom":[subQ0,sQuery(id+"F0.wireOp",EDGE,"E5.bottom")]}),1.0]])],"derivedFrom":subQ0})])],"isStart":false});}
            var Q11;
            {var subQ0=sQuery(id+"F0.wireOp",EDGE,"E5.top");Q11=makeQuery(id+"F1.opExtrude","CAP_EDGE",EDGE,{"disambiguationData":[OSD([subQ0]),TDD([makeQuery(id+"F0.imprint","IMPRINT",EDGE,{"disambiguationData":[TD([[makeQuery(id+"F0.imprint","INTERSECT",VERTEX,{"disambiguationData":[OD(1.0)],"derivedFrom":[sQuery(id+"F0.wireOp",EDGE,"E3"),subQ0]}),1.0]])],"derivedFrom":subQ0})])],"isStart":false});}
            var Q12;
            Q12=makeQuery(id+"F1.opExtrude","CAP_FACE",FACE,{"disambiguationData":[OSD([sQuery(id+"F0.wireOp",EDGE,"E1.bottom"),sQuery(id+"F0.wireOp",EDGE,"E1.top"),sQuery(id+"F0.wireOp",EDGE,"E2"),sQuery(id+"F0.wireOp",EDGE,"E3"),sQuery(id+"F0.wireOp",EDGE,"E4"),sQuery(id+"F0.wireOp",EDGE,"E5.bottom"),sQuery(id+"F0.wireOp",EDGE,"E5.top")])],"isStart":true});
            var Q13;
            Q13=makeQuery(id+"F8.hole-0.boolean.opBoolean","COPY",EDGE,{"derivedFrom":makeQuery(id+"F8.hole-0.opRevolve","SWEPT_EDGE",EDGE,{"disambiguationData":[OSD([sQuery(id+"F8.hole-0.sketch.wireOp",EDGE,"core_line_2"),sQuery(id+"F8.hole-0.sketch.wireOp",EDGE,"core_line_3")])]})});
            var Q14;
            {var subQ0=sQuery(id+"F0.wireOp",EDGE,"E2");Q14=makeQuery(id+"F1.opExtrude","CAP_EDGE",EDGE,{"disambiguationData":[OSD([subQ0]),TDD([makeQuery(id+"F0.imprint","IMPRINT",EDGE,{"disambiguationData":[TD([[makeQuery(id+"F0.imprint","INTERSECT",VERTEX,{"disambiguationData":[OD(1.0)],"derivedFrom":[sQuery(id+"F0.wireOp",EDGE,"E1.bottom"),subQ0]}),1.0]])],"derivedFrom":subQ0})])],"isStart":false});}
            var Q15;
            {var subQ0=sQuery(id+"F0.wireOp",EDGE,"E6.top");Q15=makeQuery(id+"F1.opExtrude","CAP_EDGE",EDGE,{"disambiguationData":[OSD([subQ0]),TDD([makeQuery(id+"F0.imprint","IMPRINT",EDGE,{"disambiguationData":[TD([[makeQuery(id+"F0.imprint","INTERSECT",VERTEX,{"disambiguationData":[OD(0.0)],"derivedFrom":[sQuery(id+"F0.wireOp",EDGE,"E2"),subQ0]}),1.0]])],"derivedFrom":subQ0})])],"isStart":false});}
            var Q16;
            {var subQ0=sQuery(id+"F0.wireOp",EDGE,"E4");var subQ1=makeQuery(id+"F0.imprint","INTERSECT",VERTEX,{"disambiguationData":[OD(1.0)],"derivedFrom":[subQ0,sQuery(id+"F0.wireOp",EDGE,"E5.right")]});Q16=makeQuery(id+"F1.opExtrude","CAP_EDGE",EDGE,{"disambiguationData":[OSD([subQ0]),TDD([makeQuery(id+"F0.imprint","IMPRINT",EDGE,{"disambiguationData":[TD([[makeQuery(id+"F0.imprint","INTERSECT",VERTEX,{"disambiguationData":[OD(0.0)],"derivedFrom":[subQ0,sQuery(id+"F0.wireOp",EDGE,"E6.top")]}),-1.0]])],"derivedFrom":subQ0}),makeQuery(id+"F0.imprint","IMPRINT",EDGE,{"disambiguationData":[TD([[subQ1,-1.0]])],"derivedFrom":subQ0})])],"isStart":false});}
            var Q17;
            {var subQ0=sQuery(id+"F0.wireOp",EDGE,"E6.bottom");Q17=makeQuery(id+"F1.opExtrude","CAP_EDGE",EDGE,{"disambiguationData":[OSD([subQ0]),TDD([makeQuery(id+"F0.imprint","IMPRINT",EDGE,{"disambiguationData":[TD([[makeQuery(id+"F0.imprint","INTERSECT",VERTEX,{"disambiguationData":[OD(1.0)],"derivedFrom":[sQuery(id+"F0.wireOp",EDGE,"E2"),subQ0]}),1.0]])],"derivedFrom":subQ0})])],"isStart":false});}
            var Q18;
            {var subQ0=sQuery(id+"F0.wireOp",EDGE,"E6.bottom");Q18=makeQuery(id+"F1.opExtrude","CAP_EDGE",EDGE,{"disambiguationData":[OSD([subQ0]),TDD([makeQuery(id+"F0.imprint","IMPRINT",EDGE,{"disambiguationData":[TD([[makeQuery(id+"F0.imprint","INTERSECT",VERTEX,{"disambiguationData":[OD(0.0)],"derivedFrom":[sQuery(id+"F0.wireOp",EDGE,"E2"),subQ0]}),-1.0]])],"derivedFrom":subQ0})])],"isStart":false});}
            var Q19;
            {var subQ0=sQuery(id+"F0.wireOp",EDGE,"E2");Q19=makeQuery(id+"F1.opExtrude","CAP_EDGE",EDGE,{"disambiguationData":[OSD([subQ0]),TDD([makeQuery(id+"F0.imprint","IMPRINT",EDGE,{"disambiguationData":[TD([[makeQuery(id+"F0.imprint","INTERSECT",VERTEX,{"disambiguationData":[OD(0.0)],"derivedFrom":[sQuery(id+"F0.wireOp",EDGE,"E1.bottom"),subQ0]}),-1.0]])],"derivedFrom":subQ0})])],"isStart":false});}
            var Q20;
            {var subQ0=sQuery(id+"F0.wireOp",EDGE,"E4");var subQ1=makeQuery(id+"F0.imprint","INTERSECT",VERTEX,{"disambiguationData":[OD(1.0)],"derivedFrom":[subQ0,sQuery(id+"F0.wireOp",EDGE,"E5.left")]});Q20=makeQuery(id+"F1.opExtrude","CAP_EDGE",EDGE,{"disambiguationData":[OSD([subQ0]),TDD([makeQuery(id+"F0.imprint","IMPRINT",EDGE,{"disambiguationData":[TD([[makeQuery(id+"F0.imprint","INTERSECT",VERTEX,{"disambiguationData":[OD(1.0)],"derivedFrom":[subQ0,sQuery(id+"F0.wireOp",EDGE,"E5.top")]}),-1.0]])],"derivedFrom":subQ0}),makeQuery(id+"F0.imprint","IMPRINT",EDGE,{"disambiguationData":[TD([[subQ1,-1.0]])],"derivedFrom":subQ0})])],"isStart":false});}
            var Q21;
            {var subQ0=sQuery(id+"F0.wireOp",EDGE,"E6.top");Q21=makeQuery(id+"F1.opExtrude","CAP_EDGE",EDGE,{"disambiguationData":[OSD([subQ0]),TDD([makeQuery(id+"F0.imprint","IMPRINT",EDGE,{"disambiguationData":[TD([[makeQuery(id+"F0.imprint","INTERSECT",VERTEX,{"disambiguationData":[OD(1.0)],"derivedFrom":[sQuery(id+"F0.wireOp",EDGE,"E2"),subQ0]}),-1.0]])],"derivedFrom":subQ0})])],"isStart":false});}
            fillet(context, id + "F9", {"entities" : qUnion([Q0, Q1, Q2, Q3, Q4, Q5, Q6, Q7, Q8, Q9, Q10, Q11, Q12, Q13, Q14, Q15, Q16, Q17, Q18, Q19, Q20, Q21]), "radius" : 1 * mm, "tangentPropagation" : true, "allowEdgeOverflow" : false});
        }
    });
